# Revit family: P190780JX-142c_JIC4730HS_Black-StainlessSteelTrim_JA_Cooking_Cooktops
name_source: partatom
category: Specialty Equipment
units: mm (PartAtom-declared; Revit-internal decimal feet)

## family parameters
Always vertical = Yes
Cut with Voids When Loaded = No
Enable Cutting in Views = No
Maintain Annotation Orientation = No
Part Type = Normal
Room Calculation Point = No
Round Connector Dimension = Use Diameter
Shared = No
Work Plane-Based = No

## types (1)
- JIC4730HS
    Amps = 0 A
    Body Material = ARCAT - Glass - Black
    Cooktop Edge Material = ARCAT - Metal - Steel - Stainless
    Default Elevation = 0"
    Depth = 21"
    Description = Lustre Stainless 30" Induction Flex Cooktop
Table de cuisson à induction Flex de 30 po
    Dimension Guide = https://www.whirlpool.com
https://www.whirlpool.com
    Family Name = INDUCTION UPDRAFT COOKTOP - 30"
    Feature 1 = Magnetic Induction
Induction magnétique
    Feature 2 = Razor-Fine Edge Installation
Installation de pointe
    Feature 3 = Lustre Stainless
Acier inoxydable lustré
    Height = 3/16"
    Installation-Fabrication = http://access.whirlpool.com Instruction&sku=JIC4730HS&language=EN
http://access.whirlpool.com Instruction&sku=JIC4730HS&language=EN
    Manufacturer = Jenn Air
    Model = JIC4730HS
    Voltage = 0 V
    Width = 30"

## geometry (parser evidence)
native form markers: Sweep x2
no freeform markers — native parametric forms only
